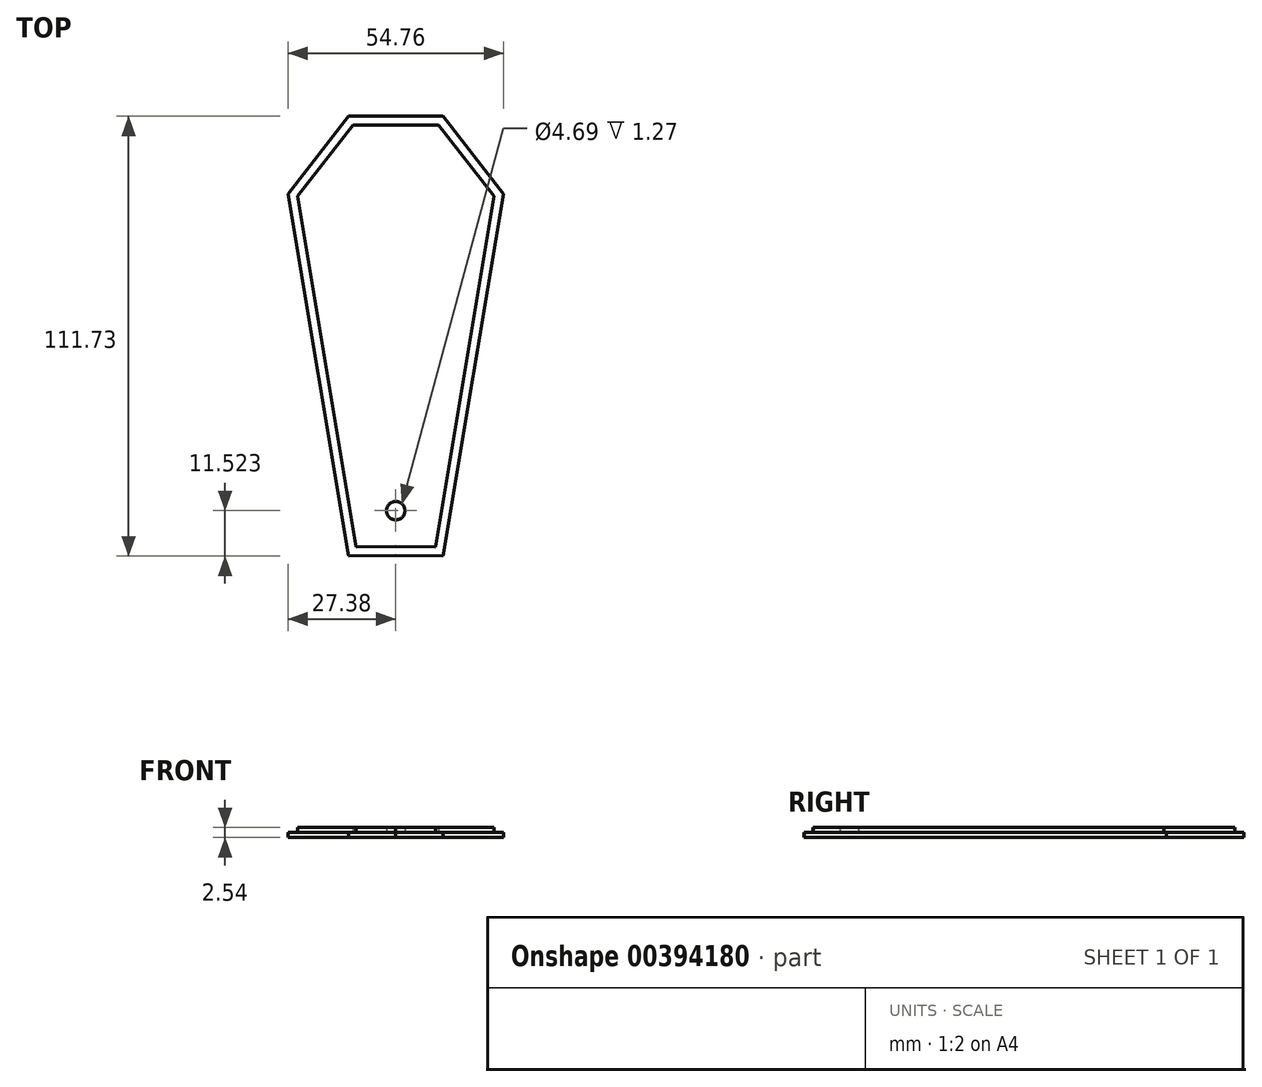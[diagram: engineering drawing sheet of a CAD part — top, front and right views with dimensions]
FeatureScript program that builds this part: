
annotation { "Feature Type Name" : "Feature", "Feature Type Description" : "" }
export const myFeature = defineFeature(function(context is Context, id is Id, definition is map)
    precondition{}
    {
        {
            var Q0;
            Q0=qCreatedBy(makeId("Top.planeOp"),FACE);
            var sketch = newSketch(context, id + "F0", { "sketchPlane" : qUnion([Q0])});
            skLineSegment(sketch, "E0", {"start": v(0, 46.8) * mm, "end": v(-12.01, 46.8) * mm});
            skLineSegment(sketch, "E1", {"start": v(-12.01, 46.8) * mm, "end": v(-27.38, 27.1) * mm});
            skLineSegment(sketch, "E2", {"start": v(-27.38, 27.1) * mm, "end": v(-12.01, -64.93) * mm});
            skLineSegment(sketch, "E3", {"start": v(-12.01, -64.93) * mm, "end": v(0, -64.74) * mm});
            skLineSegment(sketch, "E4.MirrorCS", {"start": v(27.38, 27.1) * mm, "end": v(12.01, -64.93) * mm});
            skLineSegment(sketch, "E5.MirrorCS", {"start": v(12.01, 46.8) * mm, "end": v(27.38, 27.1) * mm});
            skLineSegment(sketch, "E6.MirrorCS", {"start": v(0, 46.8) * mm, "end": v(12.01, 46.8) * mm});
            skLineSegment(sketch, "E7.MirrorCS", {"start": v(12.01, -64.93) * mm, "end": v(0, -64.74) * mm});
            skSolve(sketch);
        }
        {
            var Q0;
            Q0=makeQuery(id+"F0.imprint","IMPRINT",FACE,{"disambiguationData":[TD([[makeQuery(id+"F0.imprint","IMPRINT",EDGE,{"derivedFrom":sQuery(id+"F0.wireOp",EDGE,"E0")}),1.0]])]});
            extrude(context, id + "F1", {"entities" : qUnion([Q0]), "depth" : 1.27 * mm});
        }
        {
            var Q0;
            Q0=makeQuery(id+"F0.imprint","IMPRINT",FACE,{"disambiguationData":[TD([[makeQuery(id+"F0.imprint","IMPRINT",EDGE,{"derivedFrom":sQuery(id+"F0.wireOp",EDGE,"E0")}),1.0]])]});
            var sketch = newSketch(context, id + "F2", { "sketchPlane" : qUnion([Q0])});
            skLineSegment(sketch, "E8.0", {"start": v(10.08, -62.62) * mm, "end": v(24.96, 26.48) * mm});
            skLineSegment(sketch, "E8.1", {"start": v(0, -62.45) * mm, "end": v(10.08, -62.62) * mm});
            skLineSegment(sketch, "E8.2", {"start": v(24.96, 26.48) * mm, "end": v(10.9, 44.52) * mm});
            skLineSegment(sketch, "E8.3", {"start": v(-10.08, -62.62) * mm, "end": v(0, -62.45) * mm});
            skLineSegment(sketch, "E8.4", {"start": v(10.9, 44.52) * mm, "end": v(0, 44.52) * mm});
            skLineSegment(sketch, "E8.5", {"start": v(0, 44.52) * mm, "end": v(-10.9, 44.52) * mm});
            skLineSegment(sketch, "E8.6", {"start": v(-10.9, 44.52) * mm, "end": v(-24.96, 26.48) * mm});
            skLineSegment(sketch, "E8.7", {"start": v(-24.96, 26.48) * mm, "end": v(-10.08, -62.62) * mm});
            skLineSegment(sketch, "E9.0", {"start": v(6.65, -58.5) * mm, "end": v(20.66, 25.4) * mm});
            skLineSegment(sketch, "E9.1", {"start": v(0, -58.39) * mm, "end": v(6.65, -58.5) * mm});
            skLineSegment(sketch, "E9.2", {"start": v(20.66, 25.4) * mm, "end": v(8.91, 40.45) * mm});
            skLineSegment(sketch, "E9.3", {"start": v(-6.65, -58.5) * mm, "end": v(0, -58.39) * mm});
            skLineSegment(sketch, "E9.4", {"start": v(8.91, 40.45) * mm, "end": v(0, 40.45) * mm});
            skLineSegment(sketch, "E9.5", {"start": v(0, 40.45) * mm, "end": v(-8.91, 40.45) * mm});
            skLineSegment(sketch, "E9.6", {"start": v(-8.91, 40.45) * mm, "end": v(-20.66, 25.4) * mm});
            skLineSegment(sketch, "E9.7", {"start": v(-20.66, 25.4) * mm, "end": v(-6.65, -58.5) * mm});
            skCircle(sketch, "E10", {"center": v(0, -53.4) * mm, "radius": 2.35 * mm});
            skSolve(sketch);
        }
        {
            var Q0;
            Q0 = qSketchRegion(id + "F2", true);
            var Q1;
            Q1=makeQuery(id+"F2.imprint","IMPRINT",FACE,{"disambiguationData":[TD([[makeQuery(id+"F2.imprint","IMPRINT",EDGE,{"derivedFrom":sQuery(id+"F2.wireOp",EDGE,"E9.0")}),1.0]])]});
            extrude(context, id + "F3", {"entities" : qUnion([Q0, Q1]), "operationType" : NewBodyOperationType.ADD, "depth" : 2.54 * mm});
        }
    });
